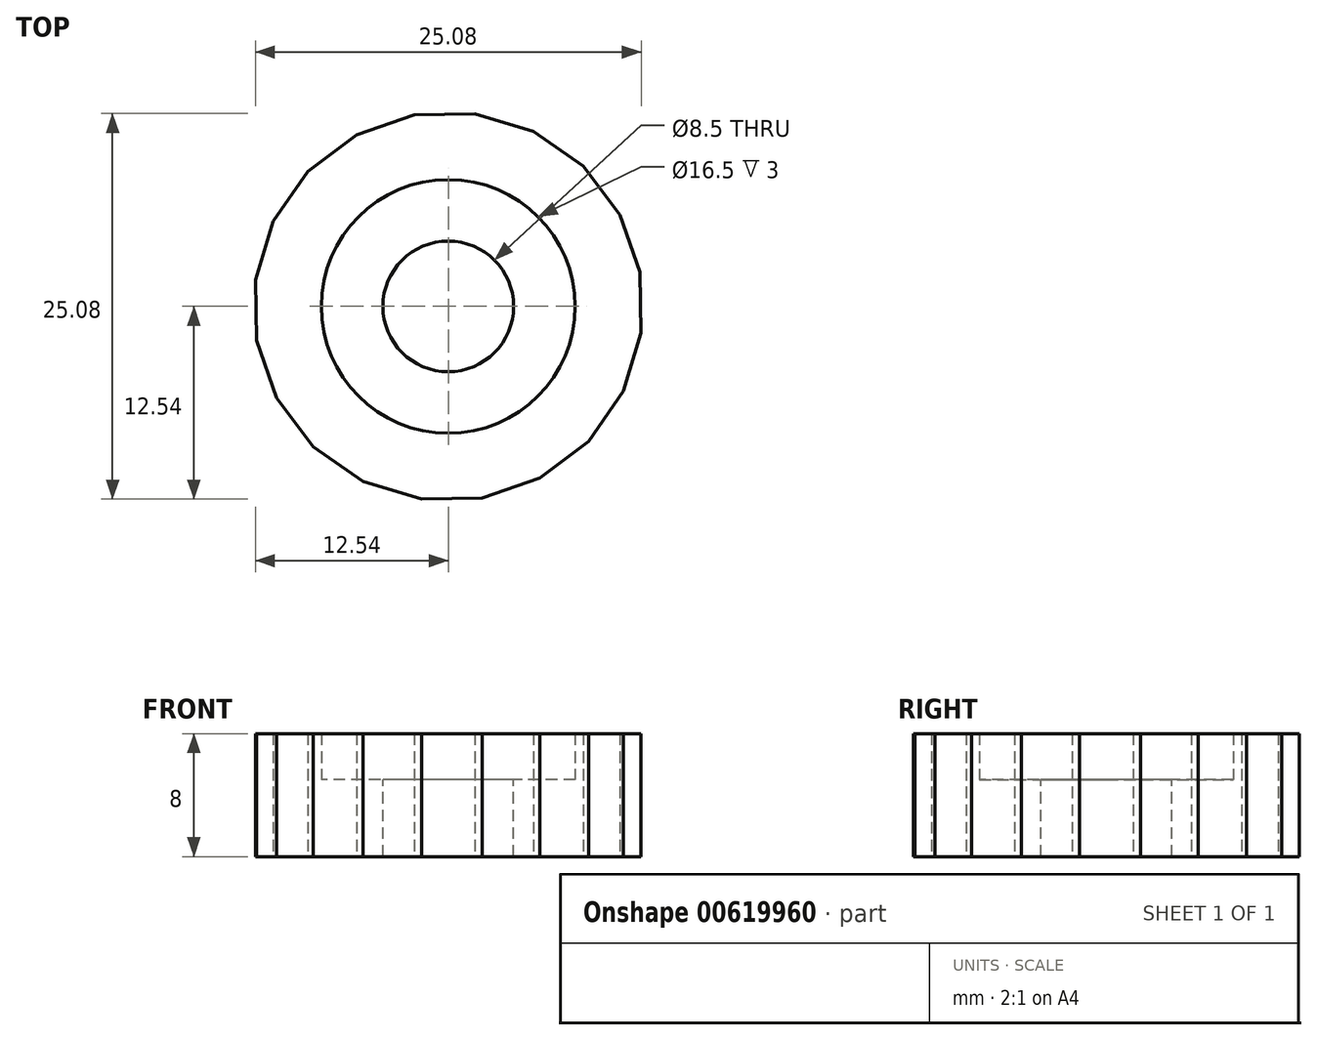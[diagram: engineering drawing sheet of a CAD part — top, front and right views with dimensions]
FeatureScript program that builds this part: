
annotation { "Feature Type Name" : "Feature", "Feature Type Description" : "" }
export const myFeature = defineFeature(function(context is Context, id is Id, definition is map)
    precondition{}
    {
        {
            var Q0;
            Q0=qCreatedBy(makeId("Top.planeOp"),FACE);
            var sketch = newSketch(context, id + "F0", { "sketchPlane" : qUnion([Q0])});
            skCircle(sketch, "E0.cCircle", {"center": v(0, 0) * mm, "radius": 12.5 * mm, "construction": true});
            skLineSegment(sketch, "E0.0", {"start": v(5.53, 11.38) * mm, "end": v(8.78, 9.12) * mm});
            skLineSegment(sketch, "E0.1", {"start": v(8.78, 9.12) * mm, "end": v(11.16, 5.96) * mm});
            skLineSegment(sketch, "E0.2", {"start": v(11.16, 5.96) * mm, "end": v(12.46, 2.22) * mm});
            skLineSegment(sketch, "E0.3", {"start": v(12.46, 2.22) * mm, "end": v(12.54, -1.74) * mm});
            skLineSegment(sketch, "E0.4", {"start": v(12.54, -1.74) * mm, "end": v(11.38, -5.53) * mm});
            skLineSegment(sketch, "E0.5", {"start": v(11.38, -5.53) * mm, "end": v(9.12, -8.78) * mm});
            skLineSegment(sketch, "E0.6", {"start": v(9.12, -8.78) * mm, "end": v(5.96, -11.16) * mm});
            skLineSegment(sketch, "E0.7", {"start": v(5.96, -11.16) * mm, "end": v(2.22, -12.46) * mm});
            skLineSegment(sketch, "E0.8", {"start": v(2.22, -12.46) * mm, "end": v(-1.74, -12.54) * mm});
            skLineSegment(sketch, "E0.9", {"start": v(-1.74, -12.54) * mm, "end": v(-5.53, -11.38) * mm});
            skLineSegment(sketch, "E0.10", {"start": v(-5.53, -11.38) * mm, "end": v(-8.78, -9.12) * mm});
            skLineSegment(sketch, "E0.11", {"start": v(-8.78, -9.12) * mm, "end": v(-11.16, -5.96) * mm});
            skLineSegment(sketch, "E0.12", {"start": v(-11.16, -5.96) * mm, "end": v(-12.46, -2.22) * mm});
            skLineSegment(sketch, "E0.13", {"start": v(-12.46, -2.22) * mm, "end": v(-12.54, 1.74) * mm});
            skLineSegment(sketch, "E0.14", {"start": v(-12.54, 1.74) * mm, "end": v(-11.38, 5.53) * mm});
            skLineSegment(sketch, "E0.15", {"start": v(-11.38, 5.53) * mm, "end": v(-9.12, 8.78) * mm});
            skLineSegment(sketch, "E0.16", {"start": v(-9.12, 8.78) * mm, "end": v(-5.96, 11.16) * mm});
            skLineSegment(sketch, "E0.17", {"start": v(-5.96, 11.16) * mm, "end": v(-2.22, 12.46) * mm});
            skLineSegment(sketch, "E0.18", {"start": v(-2.22, 12.46) * mm, "end": v(1.74, 12.54) * mm});
            skLineSegment(sketch, "E0.19", {"start": v(1.74, 12.54) * mm, "end": v(5.53, 11.38) * mm});
            skPoint(sketch, "E0.0.midPoint", {"position": v(7.15, 10.25) * mm});
            skSolve(sketch);
        }
        {
            var Q0;
            Q0=makeQuery(id+"F0.imprint","IMPRINT",FACE,{"disambiguationData":[TD([[makeQuery(id+"F0.imprint","IMPRINT",EDGE,{"derivedFrom":sQuery(id+"F0.wireOp",EDGE,"E0.0")}),-1.0]])]});
            extrude(context, id + "F1", {"entities" : qUnion([Q0]), "depth" : 5 * mm, "offsetDistance" : 25 * mm});
        }
        {
            var Q0;
            Q0=sQuery(id+"F0.wireOp",VERTEX,"E0.cCircle.center");
            var Q1;
            Q1=makeQuery(id+"F1.opExtrude","SWEPT_BODY",BODY,{"disambiguationData":[OSD([sQuery(id+"F0.wireOp",EDGE,"E0.0"),sQuery(id+"F0.wireOp",EDGE,"E0.1"),sQuery(id+"F0.wireOp",EDGE,"E0.2"),sQuery(id+"F0.wireOp",EDGE,"E0.3"),sQuery(id+"F0.wireOp",EDGE,"E0.4"),sQuery(id+"F0.wireOp",EDGE,"E0.5"),sQuery(id+"F0.wireOp",EDGE,"E0.6"),sQuery(id+"F0.wireOp",EDGE,"E0.7"),sQuery(id+"F0.wireOp",EDGE,"E0.8"),sQuery(id+"F0.wireOp",EDGE,"E0.9"),sQuery(id+"F0.wireOp",EDGE,"E0.10"),sQuery(id+"F0.wireOp",EDGE,"E0.11"),sQuery(id+"F0.wireOp",EDGE,"E0.12"),sQuery(id+"F0.wireOp",EDGE,"E0.13"),sQuery(id+"F0.wireOp",EDGE,"E0.14"),sQuery(id+"F0.wireOp",EDGE,"E0.15"),sQuery(id+"F0.wireOp",EDGE,"E0.16"),sQuery(id+"F0.wireOp",EDGE,"E0.17"),sQuery(id+"F0.wireOp",EDGE,"E0.18"),sQuery(id+"F0.wireOp",EDGE,"E0.19")])]});
            hole(context, id + "F2", {"style" : HoleStyle.SIMPLE, "endStyle" : HoleEndStyle.BLIND, "oppositeDirection" : true, "standardTappedOrClearance" : lookupTablePath({ "standard" : "ISO", "engagement" : "75%", "pitch" : "1.5 mm", "size" : "M10", "type" : "Tapped" }), "standardBlindInLast" : lookupTablePath({ "standard" : "ISO", "engagement" : "75%", "pitch" : "1.5 mm", "size" : "M10", "type" : "Tapped" }), "holeDiameter" : 8.5 * mm, "majorDiameter" : 10 * mm, "showTappedDepth" : true, "holeDepth" : 8 * mm, "isTappedThrough" : true, "tappedDepth" : 8 * mm, "tapClearance" : 0, "locations" : qUnion([Q0]), "scope" : qUnion([Q1]), "startStyle" : HoleStartStyle.SKETCH});
        }
        {
            var Q0;
            Q0=makeQuery(id+"F1.opExtrude","CAP_FACE",FACE,{"disambiguationData":[OSD([sQuery(id+"F0.wireOp",EDGE,"E0.0"),sQuery(id+"F0.wireOp",EDGE,"E0.1"),sQuery(id+"F0.wireOp",EDGE,"E0.2"),sQuery(id+"F0.wireOp",EDGE,"E0.3"),sQuery(id+"F0.wireOp",EDGE,"E0.4"),sQuery(id+"F0.wireOp",EDGE,"E0.5"),sQuery(id+"F0.wireOp",EDGE,"E0.6"),sQuery(id+"F0.wireOp",EDGE,"E0.7"),sQuery(id+"F0.wireOp",EDGE,"E0.8"),sQuery(id+"F0.wireOp",EDGE,"E0.9"),sQuery(id+"F0.wireOp",EDGE,"E0.10"),sQuery(id+"F0.wireOp",EDGE,"E0.11"),sQuery(id+"F0.wireOp",EDGE,"E0.12"),sQuery(id+"F0.wireOp",EDGE,"E0.13"),sQuery(id+"F0.wireOp",EDGE,"E0.14"),sQuery(id+"F0.wireOp",EDGE,"E0.15"),sQuery(id+"F0.wireOp",EDGE,"E0.16"),sQuery(id+"F0.wireOp",EDGE,"E0.17"),sQuery(id+"F0.wireOp",EDGE,"E0.18"),sQuery(id+"F0.wireOp",EDGE,"E0.19")])],"isStart":false});
            var sketch = newSketch(context, id + "F3", { "sketchPlane" : qUnion([Q0])});
            skCircle(sketch, "E1", {"center": v(0, 0) * mm, "radius": 8.25 * mm});
            skSolve(sketch);
        }
        {
            var Q0;
            Q0=makeQuery(id+"F3.imprint","IMPRINT",FACE,{"disambiguationData":[TD([[makeQuery(id+"F3.imprint","IMPRINT",EDGE,{"derivedFrom":sQuery(id+"F3.wireOp",EDGE,"E1")}),-1.0]])]});
            extrude(context, id + "F4", {"entities" : qUnion([Q0]), "operationType" : NewBodyOperationType.ADD, "depth" : 3 * mm, "offsetDistance" : 25 * mm});
        }
    });
